# Revit family: 20879 Шезлонг «Парабола» Хоббика
name_source: partatom
category: Антураж
revit_build: Autodesk Revit 2018 (Build: 20180423_1000(x64)
units: mm (PartAtom-declared; Revit-internal decimal feet)

## family parameters
Всегда вертикально = Да
Источник визуального образа = Геометрия семейства
На основе рабочей плоскости = Нет
Общий = Нет
При загрузке вырезать с полостями = Нет
Точка расчета площади = Нет

## types (2) — shared parameters
URL = https://hobbyka.ru
Артикул товара = Арт. 20879
Высота = 1070 мм
Группа модели = Лежаки и шезлонги
Изготовитель = ООО «Хоббика»
Изображение типоразмера = Шезлонг «Парабола» Арт 20879.jpg
Материал изделия = Сталь, дерево
Цвет каркаса = Сталь
Цвет отделки = Дерево
Ширина = 1860 мм

## per-type parameters (varying)
| type | Версия 0,8 м | Версия 1,8 м | Длина | Средняя опора |
| Шезлонг «Парабола». Версия 0,8 м | Да | Нет | 800 мм | Нет |
| Шезлонг «Парабола». Версия 1,8 м | Нет | Да | 1800 мм | Да |

note: column(s) folded — value = type name in every type: Описание
